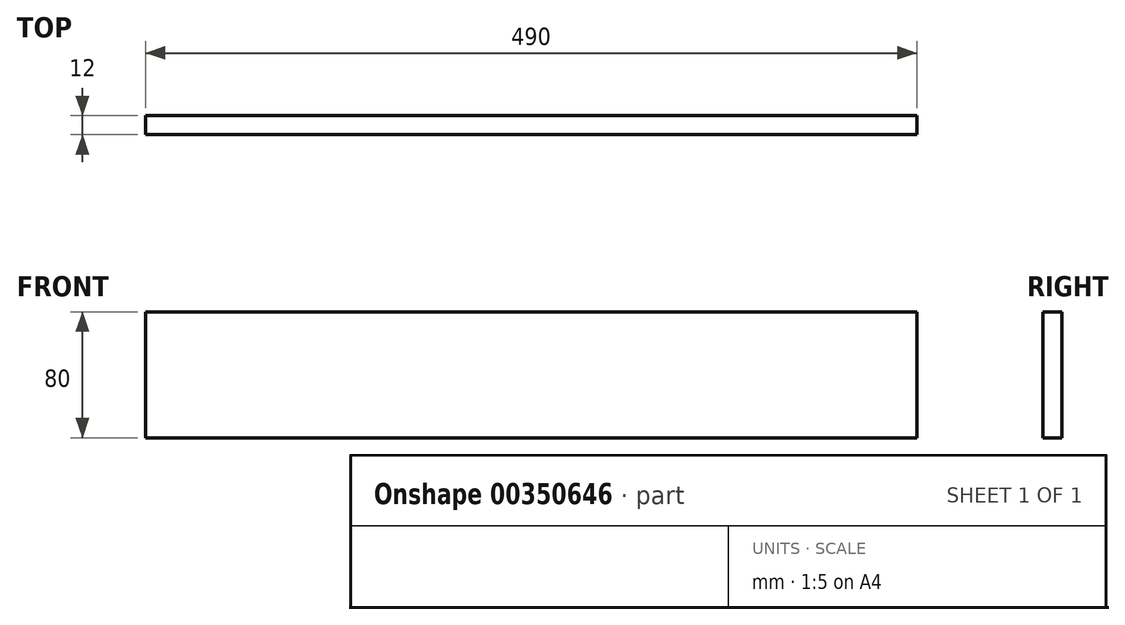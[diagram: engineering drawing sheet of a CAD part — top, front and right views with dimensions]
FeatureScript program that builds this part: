
annotation { "Feature Type Name" : "Feature", "Feature Type Description" : "" }
export const myFeature = defineFeature(function(context is Context, id is Id, definition is map)
    precondition{}
    {
        {
            var Q0;
            Q0=qCreatedBy(makeId("Front.planeOp"),FACE);
            var sketch = newSketch(context, id + "F0", { "sketchPlane" : qUnion([Q0])});
            skLineSegment(sketch, "E0.bottom", {"start": v(245, -40) * mm, "end": v(-245, -40) * mm});
            skLineSegment(sketch, "E0.top", {"start": v(245, 40) * mm, "end": v(-245, 40) * mm});
            skLineSegment(sketch, "E0.left", {"start": v(245, -40) * mm, "end": v(245, 40) * mm});
            skLineSegment(sketch, "E0.right", {"start": v(-245, -40) * mm, "end": v(-245, 40) * mm});
            skPoint(sketch, "E0.middle", {"position": v(0, 0) * mm});
            skSolve(sketch);
        }
        {
            var Q0;
            Q0=makeQuery(id+"F0.imprint","IMPRINT",FACE,{"disambiguationData":[TD([[makeQuery(id+"F0.imprint","IMPRINT",EDGE,{"derivedFrom":sQuery(id+"F0.wireOp",EDGE,"E0.bottom")}),-1.0]])]});
            extrude(context, id + "F1", {"entities" : qUnion([Q0]), "depth" : 12 * mm});
        }
    });
